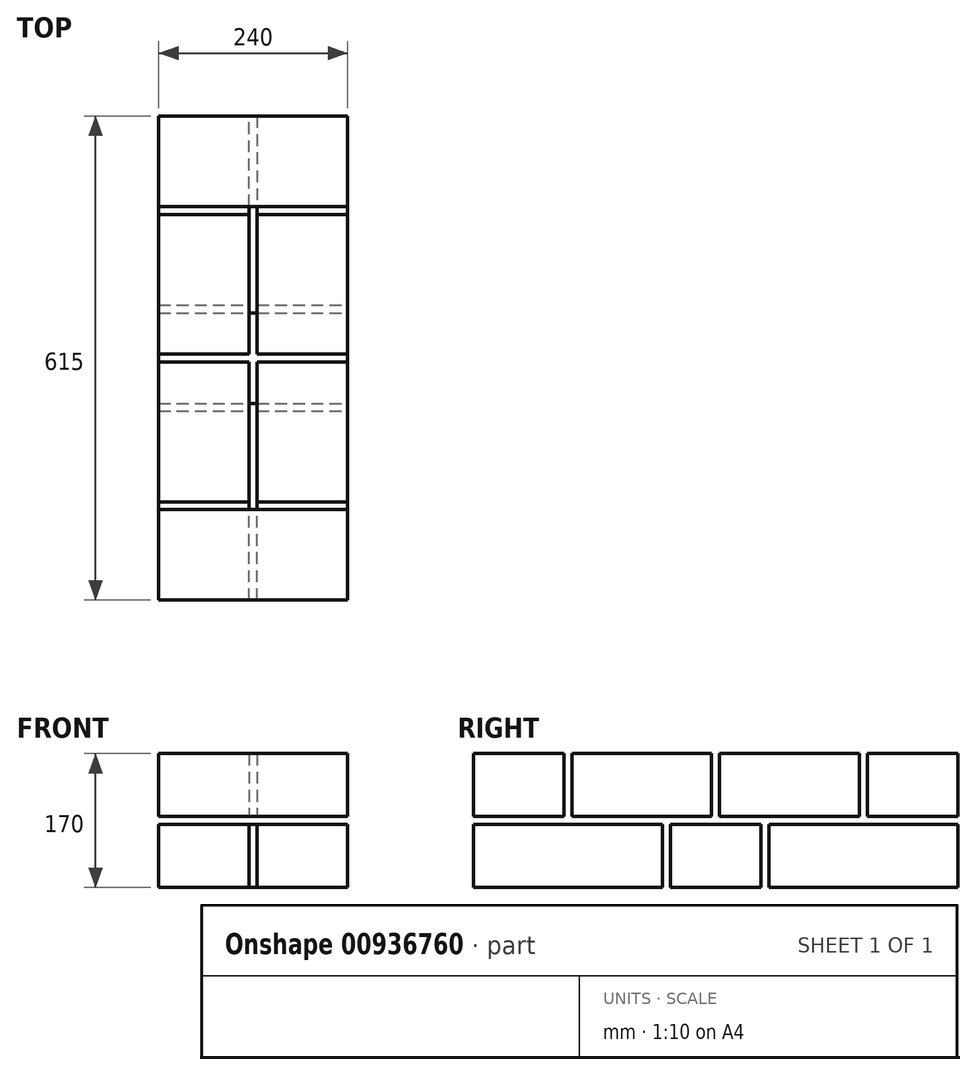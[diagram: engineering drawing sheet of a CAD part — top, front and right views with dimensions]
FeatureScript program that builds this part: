
annotation { "Feature Type Name" : "Feature", "Feature Type Description" : "" }
export const myFeature = defineFeature(function(context is Context, id is Id, definition is map)
    precondition{}
    {
        {
            var Q0;
            Q0=qCreatedBy(makeId("Top.planeOp"),FACE);
            var sketch = newSketch(context, id + "F0", { "sketchPlane" : qUnion([Q0])});
            skLineSegment(sketch, "E0.bottom", {"start": v(0, 0) * mm, "end": v(115, 0) * mm});
            skLineSegment(sketch, "E0.top", {"start": v(0, 240) * mm, "end": v(115, 240) * mm});
            skLineSegment(sketch, "E0.left", {"start": v(0, 0) * mm, "end": v(0, 240) * mm});
            skLineSegment(sketch, "E0.right", {"start": v(115, 0) * mm, "end": v(115, 240) * mm});
            skLineSegment(sketch, "E1.bottom", {"start": v(125, 0) * mm, "end": v(240, 0) * mm});
            skLineSegment(sketch, "E1.top", {"start": v(125, 240) * mm, "end": v(240, 240) * mm});
            skLineSegment(sketch, "E1.left", {"start": v(125, 0) * mm, "end": v(125, 240) * mm});
            skLineSegment(sketch, "E1.right", {"start": v(240, 0) * mm, "end": v(240, 240) * mm});
            skLineSegment(sketch, "E2.bottom", {"start": v(0, 365) * mm, "end": v(240, 365) * mm});
            skLineSegment(sketch, "E2.top", {"start": v(0, 250) * mm, "end": v(240, 250) * mm});
            skLineSegment(sketch, "E2.left", {"start": v(0, 365) * mm, "end": v(0, 250) * mm});
            skLineSegment(sketch, "E2.right", {"start": v(240, 365) * mm, "end": v(240, 250) * mm});
            skLineSegment(sketch, "E3.bottom", {"start": v(0, 375) * mm, "end": v(115, 375) * mm});
            skLineSegment(sketch, "E3.top", {"start": v(0, 615) * mm, "end": v(115, 615) * mm});
            skLineSegment(sketch, "E3.left", {"start": v(0, 375) * mm, "end": v(0, 615) * mm});
            skLineSegment(sketch, "E3.right", {"start": v(115, 375) * mm, "end": v(115, 615) * mm});
            skLineSegment(sketch, "E4.bottom", {"start": v(125, 615) * mm, "end": v(240, 615) * mm});
            skLineSegment(sketch, "E4.top", {"start": v(125, 375) * mm, "end": v(240, 375) * mm});
            skLineSegment(sketch, "E4.left", {"start": v(125, 615) * mm, "end": v(125, 375) * mm});
            skLineSegment(sketch, "E4.right", {"start": v(240, 615) * mm, "end": v(240, 375) * mm});
            skLineSegment(sketch, "E5", {"start": v(115, 0) * mm, "end": v(125, 0) * mm, "construction": true});
            skLineSegment(sketch, "E6", {"start": v(0, 240) * mm, "end": v(0, 250) * mm, "construction": true});
            skLineSegment(sketch, "E7", {"start": v(0, 365) * mm, "end": v(0, 375) * mm, "construction": true});
            skSolve(sketch);
        }
        {
            var Q0;
            Q0 = qSketchRegion(id + "F0", true);
            extrude(context, id + "F1", {"entities" : qUnion([Q0]), "depth" : 80 * mm, "offsetDistance" : 25 * mm});
        }
        {
            var Q0;
            Q0=makeQuery(id+"F1.opExtrude","CAP_FACE",FACE,{"disambiguationData":[OSD([sQuery(id+"F0.wireOp",EDGE,"E0.bottom"),sQuery(id+"F0.wireOp",EDGE,"E0.top"),sQuery(id+"F0.wireOp",EDGE,"E0.left"),sQuery(id+"F0.wireOp",EDGE,"E0.right")])],"isStart":false});
            cPlane(context, id + "F2", {"entities" : qUnion([Q0]), "cplaneType" : CPlaneType.OFFSET, "offset" : 10 * mm, "width" : 150 * mm, "height" : 150 * mm});
        }
        {
            var Q0;
            Q0=qCreatedBy(id+"F2.planeOp",FACE);
            var sketch = newSketch(context, id + "F3", { "sketchPlane" : qUnion([Q0])});
            skLineSegment(sketch, "E8.bottom", {"start": v(0, 0) * mm, "end": v(240, 0) * mm});
            skLineSegment(sketch, "E8.top", {"start": v(0, 115) * mm, "end": v(240, 115) * mm});
            skLineSegment(sketch, "E8.left", {"start": v(0, 0) * mm, "end": v(0, 115) * mm});
            skLineSegment(sketch, "E8.right", {"start": v(240, 0) * mm, "end": v(240, 115) * mm});
            skLineSegment(sketch, "E9.bottom", {"start": v(0, 125) * mm, "end": v(115, 125) * mm});
            skLineSegment(sketch, "E9.top", {"start": v(0, 302.5) * mm, "end": v(115, 302.5) * mm});
            skLineSegment(sketch, "E9.left", {"start": v(0, 125) * mm, "end": v(0, 302.5) * mm});
            skLineSegment(sketch, "E9.right", {"start": v(115, 125) * mm, "end": v(115, 302.5) * mm});
            skLineSegment(sketch, "E10.bottom", {"start": v(240, 125) * mm, "end": v(125, 125) * mm});
            skLineSegment(sketch, "E10.top", {"start": v(240, 302.5) * mm, "end": v(125, 302.5) * mm});
            skLineSegment(sketch, "E10.left", {"start": v(240, 125) * mm, "end": v(240, 302.5) * mm});
            skLineSegment(sketch, "E10.right", {"start": v(125, 125) * mm, "end": v(125, 302.5) * mm});
            skLineSegment(sketch, "E11.bottom", {"start": v(0, 312.5) * mm, "end": v(115, 312.5) * mm});
            skLineSegment(sketch, "E11.top", {"start": v(0, 490) * mm, "end": v(115, 490) * mm});
            skLineSegment(sketch, "E11.left", {"start": v(0, 312.5) * mm, "end": v(0, 490) * mm});
            skLineSegment(sketch, "E11.right", {"start": v(115, 312.5) * mm, "end": v(115, 490) * mm});
            skLineSegment(sketch, "E12.bottom", {"start": v(125, 490) * mm, "end": v(240, 490) * mm});
            skLineSegment(sketch, "E12.top", {"start": v(125, 312.5) * mm, "end": v(240, 312.5) * mm});
            skLineSegment(sketch, "E12.left", {"start": v(125, 490) * mm, "end": v(125, 312.5) * mm});
            skLineSegment(sketch, "E12.right", {"start": v(240, 490) * mm, "end": v(240, 312.5) * mm});
            skLineSegment(sketch, "E13.bottom", {"start": v(0, 615) * mm, "end": v(240, 615) * mm});
            skLineSegment(sketch, "E13.top", {"start": v(0, 500) * mm, "end": v(240, 500) * mm});
            skLineSegment(sketch, "E13.left", {"start": v(0, 615) * mm, "end": v(0, 500) * mm});
            skLineSegment(sketch, "E13.right", {"start": v(240, 615) * mm, "end": v(240, 500) * mm});
            skLineSegment(sketch, "E14", {"start": v(0, 115) * mm, "end": v(0, 125) * mm, "construction": true});
            skLineSegment(sketch, "E15", {"start": v(0, 302.5) * mm, "end": v(0, 312.5) * mm, "construction": true});
            skLineSegment(sketch, "E16", {"start": v(0, 490) * mm, "end": v(0, 500) * mm, "construction": true});
            skSolve(sketch);
        }
        {
            var Q0;
            Q0 = qSketchRegion(id + "F3", true);
            extrude(context, id + "F4", {"entities" : qUnion([Q0]), "depth" : 80 * mm, "offsetDistance" : 25 * mm});
        }
    });
